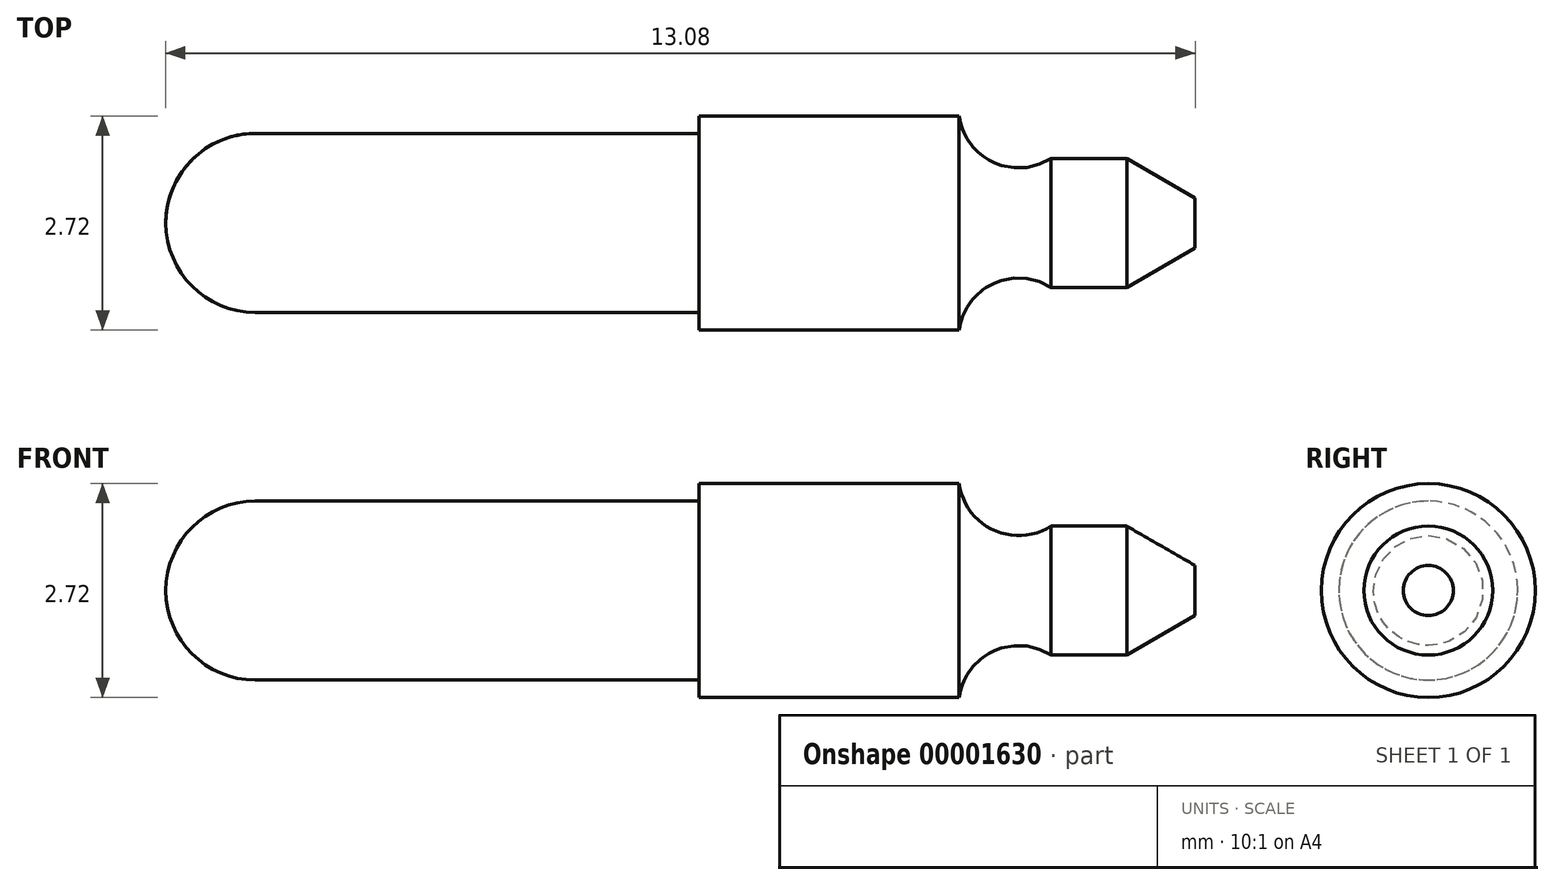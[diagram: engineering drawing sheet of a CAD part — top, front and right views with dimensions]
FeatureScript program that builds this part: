
annotation { "Feature Type Name" : "Feature", "Feature Type Description" : "" }
export const myFeature = defineFeature(function(context is Context, id is Id, definition is map)
    precondition{}
    {
        {
            var Q0;
            Q0=qCreatedBy(makeId("Top.planeOp"),FACE);
            var sketch = newSketch(context, id + "F0", { "sketchPlane" : qUnion([Q0])});
            skArc(sketch, "E0", {"start": v(0, 1.14) * mm, "mid": v(-0.8, 0.8) * mm, "end": v(-1.14, 0) * mm});
            skLineSegment(sketch, "E1", {"start": v(0, 0) * mm, "end": v(1.14, 0) * mm});
            skLineSegment(sketch, "E2", {"start": v(1.14, 0) * mm, "end": v(11.94, 0) * mm});
            skLineSegment(sketch, "E3", {"start": v(0, 1.14) * mm, "end": v(5.64, 1.14) * mm});
            skLineSegment(sketch, "E4", {"start": v(5.64, 1.14) * mm, "end": v(5.64, 1.36) * mm});
            skLineSegment(sketch, "E5", {"start": v(5.64, 1.36) * mm, "end": v(8.94, 1.36) * mm});
            skLineSegment(sketch, "E6", {"start": v(11.94, 0) * mm, "end": v(11.94, 0.32) * mm});
            skLineSegment(sketch, "E7", {"start": v(11.94, 0.32) * mm, "end": v(11.07, 0.82) * mm});
            skLineSegment(sketch, "E8", {"start": v(11.07, 0.82) * mm, "end": v(10.1, 0.82) * mm});
            skArc(sketch, "E9", {"start": v(8.94, 1.36) * mm, "mid": v(9.38, 0.77) * mm, "end": v(10.1, 0.82) * mm});
            skLineSegment(sketch, "E10", {"start": v(0, 0) * mm, "end": v(-1.14, 0) * mm});
            skSolve(sketch);
        }
        {
            var Q0;
            Q0=makeQuery(id+"F0.imprint","IMPRINT",FACE,{"disambiguationData":[TD([[makeQuery(id+"F0.imprint","IMPRINT",EDGE,{"derivedFrom":sQuery(id+"F0.wireOp",EDGE,"E0")}),1.0]])]});
            var Q1;
            Q1=sQuery(id+"F0.wireOp",EDGE,"E2");
            revolve(context, id + "F1", {"entities" : qUnion([Q0]), "axis" : qUnion([Q1]), "revolveType" : RevolveType.FULL});
        }
    });
